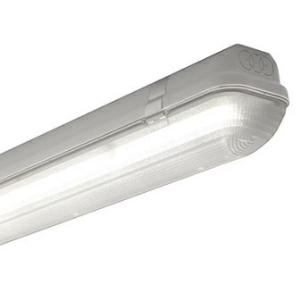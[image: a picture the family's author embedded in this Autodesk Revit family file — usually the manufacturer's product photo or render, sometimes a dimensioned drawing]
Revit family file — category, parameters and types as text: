
# Revit family: 3f_filippi_-_3f_linda_hq_3f_filippi_-_58877_-_3f_linda_led_1x30w-940_dali_l1570
name_source: partatom
category: Lighting Fixtures
units: mm (PartAtom-declared; Revit-internal decimal feet)

## family parameters
Cut with Voids When Loaded = No
Host = Face
Light Source = No
Part Type = Normal
Room Calculation Point = No
Round Connector Dimension = Use Diameter
Shared = No

## types (1)
- 3F Filippi - 3F Linda HQ (1 x LED, 4015 lm, 33.5 W, 4000 K)
    Apparent Load = 34 VA
    Approval mark = CE
    CIE Flux Codes = 44 77 94 97 100
    Color Rendering = 90
    Color Temperature = 4000 K
    Control Gear = Electronic transformer
    Default Elevation = 1800 mm
    Description = ILLUMINOTECHNICAL
Luminous efficiency 100% (DLOR 97%, ULOR 3%).
Initial luminous flux of the luminaire 4015 lm.
Controlled symmetric distribution.
Installation Interdistance Transv.D = 1.77 x hu - Long.D = 1.17 x hu.
Tabular UGR (CIE 117 - 4H-8H; S=0.25H; 70/50/20): RUG 21.2 - 22.2.
Beam angle: 109° - 64°.
Luminous efficacy 120 lm/W.
Lifetime (L93/B10): 30000 h. (tq+25°C)
Lifetime (L90/B10): 50000 h. (tq+25°C)
Lifetime (L85/B10): 80000 h. (tq+25°C)
Lifetime (L80/B10): 100000 h. (tq+25°C)
Lifetime (L85/B10): 50000 h. (tq+35°C)
Sudden decreased luminous flux after 50000 hours: 0% (C0).
Photobiological safety in compliance with IEC/TR 62778: RG0 risk exempt, (IEC 62471).
In compliance with IEC/EN 62722-2-1 - IEC/EN 62717 standards.

SOURCE
Linear LED module 30W/940.
Energy efficiency class (UE 2019/2020 - UE 2019/2015): E.
CIE 13.3 Colour rendering index: CRI >90 (R9 >50%).
IES TM-30 Fidelity Index: Rf = 92 Rg = 101.
CCT nominal colour temperature 4000 K.
Colour initial tolerance (MacAdam): SDCM 3.

MECHANICAL
Self-extinguishing V2 polycarbonate housing, injection moulded, RAL 7035 grey.
Ecologic anti-aging injected sealing gasket.
Diffuser in self-extinguishing V2 polycarbonate, photo-engraved interior, UV stabilised, injection moulded with smooth outer surface, tamper-proof opening.
Gear-holder reflector in hot-dip galvanised steel, painted with white polyester base.
Snug fit safety snap-lock clips for diffuser mounting in stainless steel, screwdriver opening.
Fixing brackets in stainless steel.
Possibility for technicians to access the interior of the luminaire.
Luminaire with limited surface temperature. - D - (EN 60598-2-24)
Dimensions: 1570x100 mm, height 100 mm. Weight 2.57 kg.
IP66 protection degree.
Mechanical strength to impacts IK10 (20 joule).
Glow-wire test resistance 850°C.

ELECTRICAL
Halogen Free DALI-2 DATI (Parts 251, 252, 253), PUSH-DIM, electronic wiring 230V-50/60Hz, power factor 0.95 at full load, THD <25%, constant output current, SELV, class I, 1 driver, 1 DALI addresse.
Power of the luminaire 33.5 W.
ENEC - CE.
SAFE FLICKER: PstLM=<1 and SVM=<0.4 (IEC TR 61547-1 and IEC TR 63158), to ensure a more comfortable and safe light.
Luminaire compliant with EN 60598-2-22 for power supply from a centralised emergency system CPSS (Central Power Supply System), not incorporated in the luminaire - high risk areas excluded. The default power and flux are 100% in AC and 15% in DC.
Ambient temperature from -20°C to +35°C.
Temperature class T6 max 85°C.
Relative humidity UR: <85%.

INSTALLATION
Ceiling / Suspended / Wall.
All accessories dedicated to this product are available on the Catalog and on our website www.3F-Filippi.com.

APPLICATIONS
Suitable product for food production plants (HACCP), IFS (Food Version 6), BRC (GSFS Food Version 7).
Dry, dusty indoor environments, subject to occasional water splashes.
Virtually shatterproof polycarbonate compatibly with the fumes / atmospheres that compromise the elasticity of plastic materials.
Not suitable for installation on surfaces subject to important vibrations, exposed to weather conditions, on ropes or poles.
Suitable for illumination of public car parks and parking grounds referred to DIN 67528:2018-04.

LIGHT MANAGEMENT
Recommended minimum setting: 10%.
The luminaire, equipped with (DALI-2 DATI) driver, can be controlled manually with 3F Easy Dim technology or automatically/manually with wired or wireless DALI/D2D control systems.
The D2D driver guarantees interoperability with other devices with the same certification by making the following information available:
Device Data (Part 251), Energy Report (Part 252), Diagnosis & Maintenance (Part 253).
In electrical systems without a regulation system (manual or automatic) and DALI bus, a suitable jumper must be made on the DA-DA terminals of the appliance.

WARNING
Fixture not suitable for cold stores with an ambient temperature <0°C and/or relative humidity >85%.
Luminaire designed for disposal/recycling at end-of-life.
Replaceable (LED only) light source by a professional. Replaceable control gear by a professional.
    Height = 100 mm  [stored 0.328084 ft]
    Lamp = 1 x LED
    Lamp Light Flux = 4015 lm
    Lamp Power = 33.5 W
    Lamp count = 1
    Length = 1570 mm
    Lifetime = 50000 h
    Luminous efficacy = 120 lm/W
    Manufacturer = 3F Filippi
    ModVariant = No
    Model = 3F Filippi - 58877 - 3F Linda LED 1x30W-940 DALI L1570
    Mounting Place = Ceiling
    Mounting Type = Pendant
    Number of Poles = 1
    OnlyDefault = Yes
    Power Factor = 1
    Product Name = 3F Filippi - 3F Linda HQ
    Product group = pendant luminaire
    ProductGroupID = 9
    Protection Class = Protection class I
    Protection Degree = IP 66
    RLX_Detail_Level = 1
    RLX_Emergency_Light_Flux = 0 lm
    RLX_Emergency_Type = 0
    RLX_Emergency_Type_DB = No
    RlxData = <blob elided: 71053 chars, md5=dc33ef6b>
    Socket = socket
    Standby Power = 0 W
    System Light Flux = 4015 lm
    System Power = 34 W
    Type Comments = Product without accessories
    Type Image = 3ffilippi_3f_linda_led_1x.jpg
    URL = http://relux.com
    VarID = ---
    Voltage = 0 V
    Weight = 0.00 kg
    Width = 100 mm  [stored 0.328084 ft]

note: [stored X ft] marks values corroborated as IEEE doubles in the binary element streams (Revit-internal decimal feet)

## geometry (parser evidence)
native form markers: Blend x4, Sweep x9
no freeform markers — native parametric forms only
